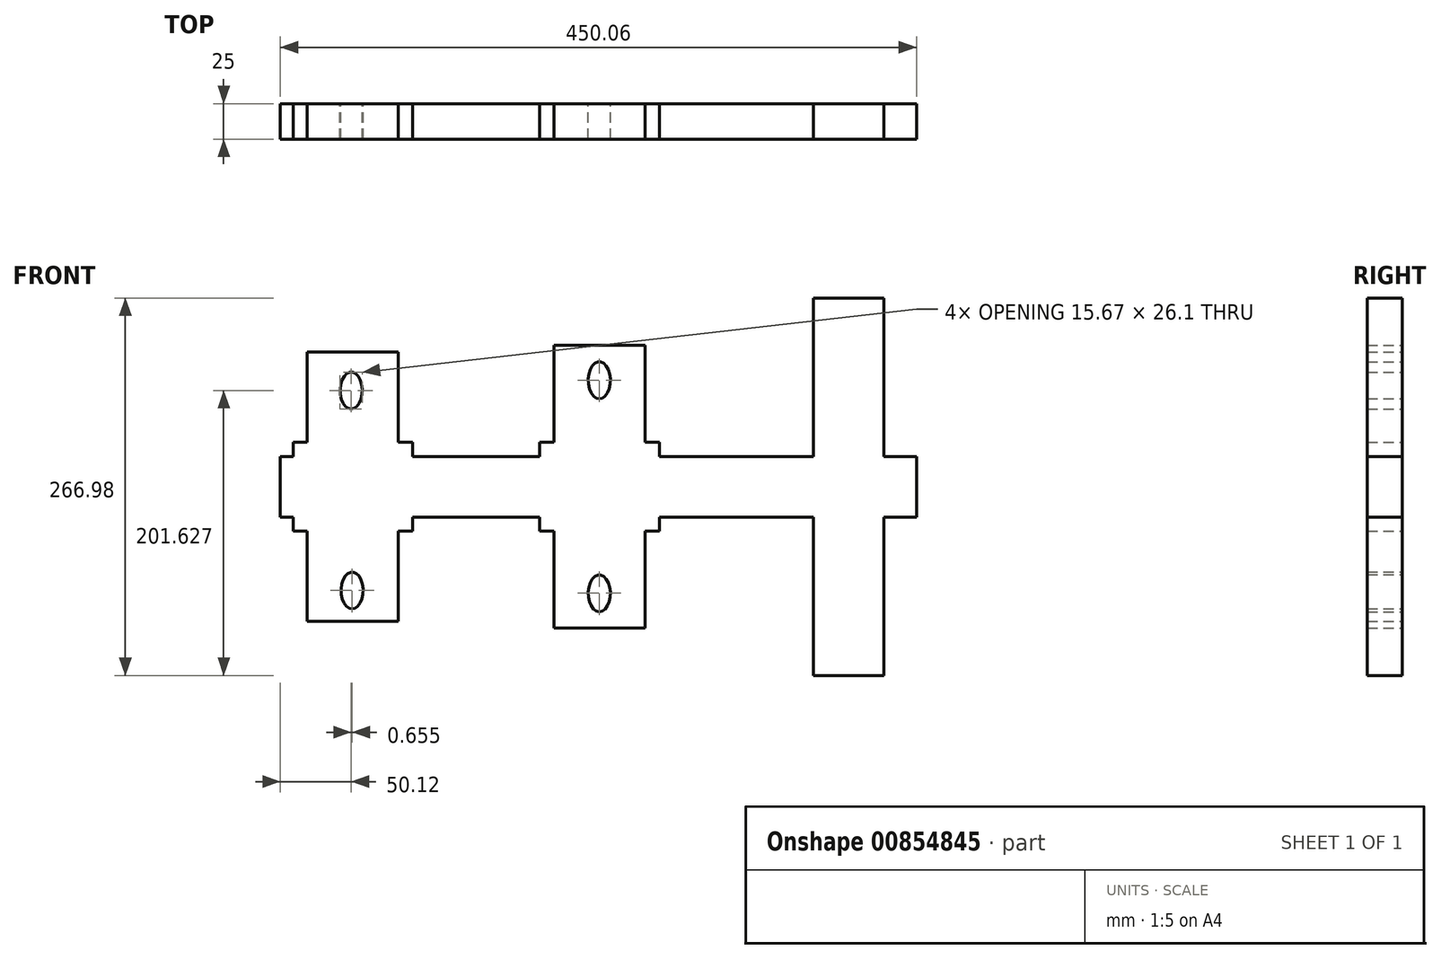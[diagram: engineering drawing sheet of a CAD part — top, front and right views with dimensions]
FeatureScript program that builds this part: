
annotation { "Feature Type Name" : "Feature", "Feature Type Description" : "" }
export const myFeature = defineFeature(function(context is Context, id is Id, definition is map)
    precondition{}
    {
        {
            var Q0;
            Q0=qCreatedBy(makeId("Front.planeOp"),FACE);
            var sketch = newSketch(context, id + "F0", { "sketchPlane" : qUnion([Q0])});
            skLineSegment(sketch, "E0", {"start": v(334.52, 0) * mm, "end": v(334.52, 21.4) * mm});
            skLineSegment(sketch, "E1", {"start": v(334.52, 21.4) * mm, "end": v(311.52, 21.4) * mm});
            skLineSegment(sketch, "E2", {"start": v(311.52, 0) * mm, "end": v(311.52, 133.49) * mm});
            skLineSegment(sketch, "E3", {"start": v(311.52, 133.49) * mm, "end": v(261.52, 133.49) * mm});
            skLineSegment(sketch, "E4", {"start": v(261.52, 133.49) * mm, "end": v(261.52, 0) * mm});
            skLineSegment(sketch, "E5", {"start": v(152.52, 21.4) * mm, "end": v(152.52, 31.4) * mm});
            skLineSegment(sketch, "E6", {"start": v(152.52, 31.4) * mm, "end": v(142.52, 31.4) * mm});
            skLineSegment(sketch, "E7", {"start": v(142.52, 31.4) * mm, "end": v(142.52, 100) * mm});
            skLineSegment(sketch, "E8", {"start": v(142.52, 100) * mm, "end": v(78.02, 100) * mm});
            skLineSegment(sketch, "E9", {"start": v(78.02, 100) * mm, "end": v(78.02, 31.4) * mm});
            skPoint(sketch, "E10.end.orphan", {"position": v(-21.98, 21.4) * mm});
            skLineSegment(sketch, "E11", {"start": v(142.52, 31.4) * mm, "end": v(142.52, 0) * mm});
            skLineSegment(sketch, "E12", {"start": v(152.52, 21.4) * mm, "end": v(152.52, 0) * mm});
            skLineSegment(sketch, "E13", {"start": v(78.02, 31.4) * mm, "end": v(78.02, 0) * mm});
            skLineSegment(sketch, "E14", {"start": v(78.02, 31.4) * mm, "end": v(68.02, 31.4) * mm});
            skLineSegment(sketch, "E15", {"start": v(68.02, 31.4) * mm, "end": v(68.02, 0) * mm});
            skLineSegment(sketch, "E16", {"start": v(68.02, 21.4) * mm, "end": v(-21.98, 21.4) * mm});
            skLineSegment(sketch, "E17", {"start": v(-21.98, 0) * mm, "end": v(-21.98, 31.4) * mm});
            skLineSegment(sketch, "E18", {"start": v(-21.98, 31.4) * mm, "end": v(-31.98, 31.4) * mm});
            skLineSegment(sketch, "E19", {"start": v(-31.98, 31.4) * mm, "end": v(-31.98, 0) * mm});
            skLineSegment(sketch, "E20", {"start": v(-31.98, 31.4) * mm, "end": v(-31.98, 95.27) * mm});
            skLineSegment(sketch, "E21", {"start": v(-31.98, 95.27) * mm, "end": v(-96.48, 95.27) * mm});
            skLineSegment(sketch, "E22", {"start": v(-96.48, 95.27) * mm, "end": v(-96.48, 0) * mm});
            skLineSegment(sketch, "E23", {"start": v(-96.48, 31.4) * mm, "end": v(-106.48, 31.4) * mm});
            skLineSegment(sketch, "E24", {"start": v(-106.48, 31.4) * mm, "end": v(-106.48, 0) * mm});
            skLineSegment(sketch, "E25", {"start": v(-106.48, 21.4) * mm, "end": v(-115.54, 21.4) * mm});
            skPoint(sketch, "E25.startSnap0", {"position": v(-106.48, 15.7) * mm});
            skLineSegment(sketch, "E26", {"start": v(-115.54, 21.4) * mm, "end": v(-115.48, 0) * mm});
            skPoint(sketch, "E27.orphan", {"position": v(-64.56, 21.4) * mm});
            skLineSegment(sketch, "E28.MirrorCS", {"start": v(78.02, -31.4) * mm, "end": v(68.02, -31.4) * mm});
            skLineSegment(sketch, "E29.MirrorCS", {"start": v(152.52, -31.4) * mm, "end": v(142.52, -31.4) * mm});
            skLineSegment(sketch, "E30.MirrorCS", {"start": v(-106.48, -21.4) * mm, "end": v(-115.54, -21.4) * mm});
            skLineSegment(sketch, "E31.MirrorCS", {"start": v(152.52, -21.4) * mm, "end": v(152.52, -31.4) * mm});
            skLineSegment(sketch, "E32.MirrorCS", {"start": v(-21.98, -31.4) * mm, "end": v(-31.98, -31.4) * mm});
            skLineSegment(sketch, "E33.MirrorCS", {"start": v(-106.48, -31.4) * mm, "end": v(-106.48, 0) * mm});
            skLineSegment(sketch, "E34.MirrorCS", {"start": v(-96.48, -31.4) * mm, "end": v(-106.48, -31.4) * mm});
            skLineSegment(sketch, "E35.MirrorCS", {"start": v(-115.54, -21.4) * mm, "end": v(-115.48, 0) * mm});
            skLineSegment(sketch, "E36.MirrorCS", {"start": v(311.52, 0) * mm, "end": v(311.52, -133.49) * mm});
            skLineSegment(sketch, "E37.MirrorCS", {"start": v(-31.98, -95.27) * mm, "end": v(-96.48, -95.27) * mm});
            skLineSegment(sketch, "E38.MirrorCS", {"start": v(334.52, 0) * mm, "end": v(334.52, -21.4) * mm});
            skLineSegment(sketch, "E39.MirrorCS", {"start": v(-21.98, 0) * mm, "end": v(-21.98, -31.4) * mm});
            skPoint(sketch, "E40.MirrorP", {"position": v(-106.48, -15.7) * mm});
            skLineSegment(sketch, "E41.MirrorCS", {"start": v(-96.48, -95.27) * mm, "end": v(-96.48, 0) * mm});
            skLineSegment(sketch, "E42.MirrorCS", {"start": v(68.02, -21.4) * mm, "end": v(-21.98, -21.4) * mm});
            skLineSegment(sketch, "E43.MirrorCS", {"start": v(261.52, -133.49) * mm, "end": v(261.52, 0) * mm});
            skLineSegment(sketch, "E44.MirrorCS", {"start": v(-31.98, -31.4) * mm, "end": v(-31.98, 0) * mm});
            skLineSegment(sketch, "E45.MirrorCS", {"start": v(78.02, -100) * mm, "end": v(78.02, -31.4) * mm});
            skLineSegment(sketch, "E46.MirrorCS", {"start": v(142.52, -31.4) * mm, "end": v(142.52, 0) * mm});
            skLineSegment(sketch, "E47.MirrorCS", {"start": v(152.52, -21.4) * mm, "end": v(152.52, 0) * mm});
            skLineSegment(sketch, "E48.MirrorCS", {"start": v(142.52, -100) * mm, "end": v(78.02, -100) * mm});
            skLineSegment(sketch, "E49.MirrorCS", {"start": v(334.52, -21.4) * mm, "end": v(311.52, -21.4) * mm});
            skLineSegment(sketch, "E50.MirrorCS", {"start": v(68.02, -31.4) * mm, "end": v(68.02, 0) * mm});
            skLineSegment(sketch, "E51.MirrorCS", {"start": v(142.52, -31.4) * mm, "end": v(142.52, -100) * mm});
            skPoint(sketch, "E52.MirrorP", {"position": v(-64.56, -21.4) * mm});
            skLineSegment(sketch, "E53.MirrorCS", {"start": v(78.02, -31.4) * mm, "end": v(78.02, 0) * mm});
            skLineSegment(sketch, "E54.MirrorCS", {"start": v(-31.98, -31.4) * mm, "end": v(-31.98, -95.27) * mm});
            skLineSegment(sketch, "E55.MirrorCS", {"start": v(311.52, -133.49) * mm, "end": v(261.52, -133.49) * mm});
            skPoint(sketch, "E56.MirrorP", {"position": v(-21.98, -21.4) * mm});
            skLineSegment(sketch, "E57.trimOffspring", {"start": v(261.52, 21.4) * mm, "end": v(152.52, 21.4) * mm});
            skLineSegment(sketch, "E58.trimOffspring", {"start": v(261.52, -21.4) * mm, "end": v(152.52, -21.4) * mm});
            skPoint(sketch, "E59.oppositeSnap0", {"position": v(-64.23, 95.27) * mm});
            skEllipse(sketch, "E60", {"center": v(-65.42, 68.14) * mm, "majorRadius": 13.05 * mm, "minorRadius": 7.84 * mm, "majorAxis": v(0, -1)});
            skEllipse(sketch, "E61", {"center": v(-64.77, -73.3) * mm, "majorRadius": 13.05 * mm, "minorRadius": 7.84 * mm, "majorAxis": v(0, -1)});
            skEllipse(sketch, "E62", {"center": v(110.08, 75.34) * mm, "majorRadius": 13.05 * mm, "minorRadius": 7.84 * mm, "majorAxis": v(0, -1)});
            skEllipse(sketch, "E63", {"center": v(110.08, -75.27) * mm, "majorRadius": 13.05 * mm, "minorRadius": 7.84 * mm, "majorAxis": v(0, -1)});
            skSolve(sketch);
        }
        {
            var Q0;
            Q0 = qSketchRegion(id + "F0", true);
            extrude(context, id + "F1", {"entities" : qUnion([Q0]), "depth" : 25 * mm, "offsetDistance" : 25 * mm});
        }
        {
            var Q0;
            Q0 = qSketchRegion(id + "F0", true);
            extrude(context, id + "F2", {"entities" : qUnion([Q0]), "operationType" : NewBodyOperationType.ADD, "depth" : 25 * mm, "offsetDistance" : 25 * mm});
        }
    });
